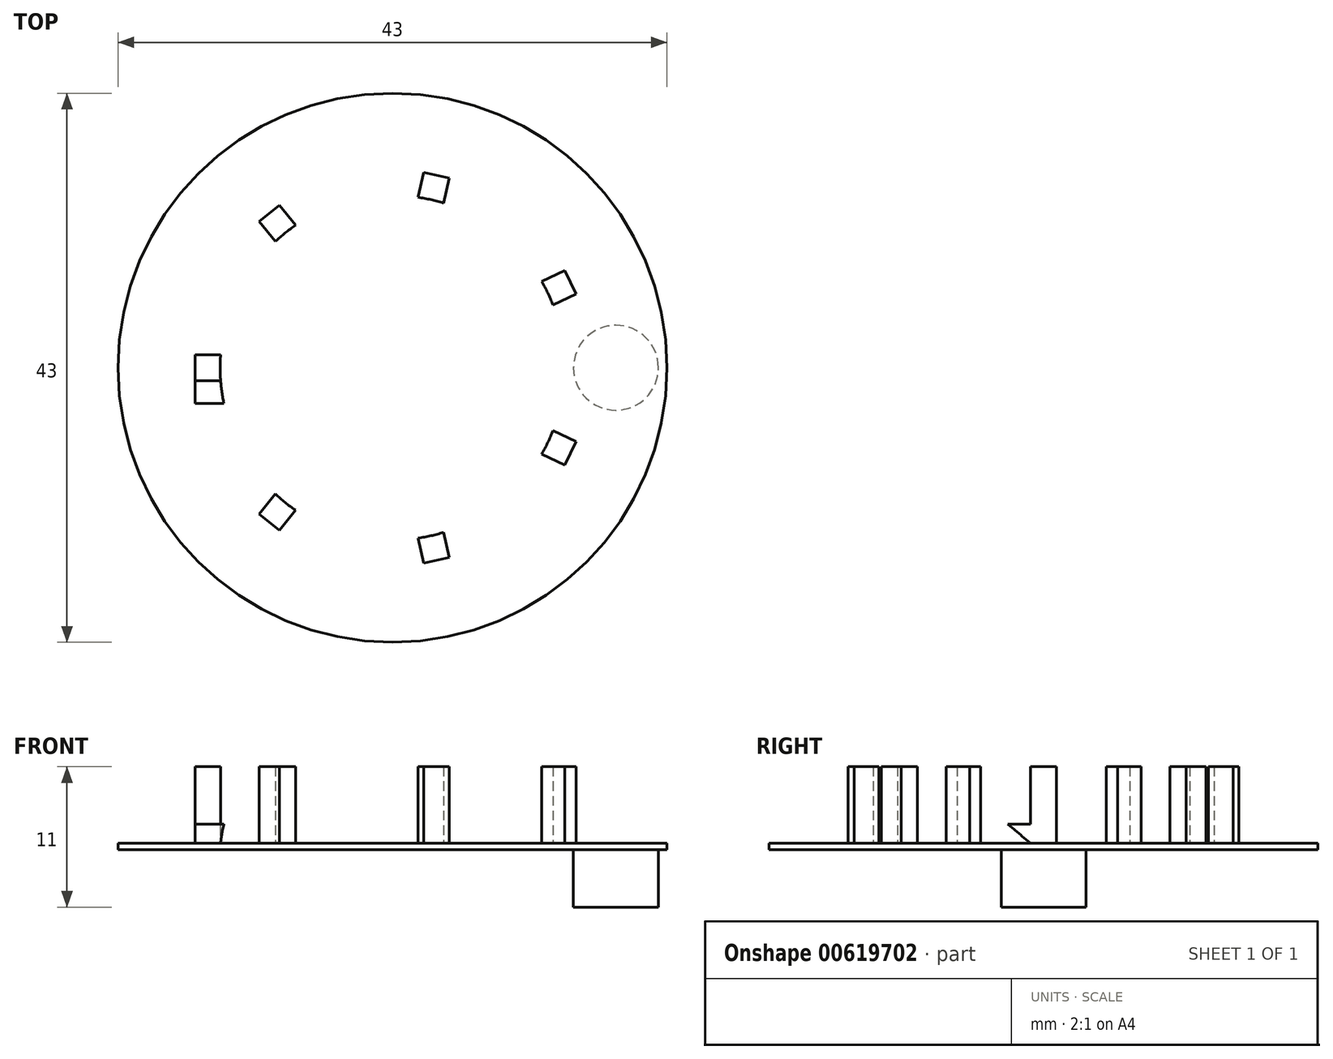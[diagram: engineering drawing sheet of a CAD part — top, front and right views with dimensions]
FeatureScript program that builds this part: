
annotation { "Feature Type Name" : "Feature", "Feature Type Description" : "" }
export const myFeature = defineFeature(function(context is Context, id is Id, definition is map)
    precondition{}
    {
        {
            var Q0;
            Q0=qCreatedBy(makeId("Top.planeOp"),FACE);
            var sketch = newSketch(context, id + "F0", { "sketchPlane" : qUnion([Q0])});
            skCircle(sketch, "E0", {"center": v(0, 0) * mm, "radius": 13.5 * mm});
            skCircle(sketch, "E1", {"center": v(0, 0) * mm, "radius": 21.5 * mm});
            skSolve(sketch);
        }
        {
            var Q0;
            Q0=makeQuery(id+"F0.imprint","IMPRINT",FACE,{"disambiguationData":[TD([[makeQuery(id+"F0.imprint","IMPRINT",EDGE,{"derivedFrom":sQuery(id+"F0.wireOp",EDGE,"E0")}),-1.0]])]});
            var Q1;
            Q1=makeQuery(id+"F0.imprint","IMPRINT",FACE,{"disambiguationData":[TD([[makeQuery(id+"F0.imprint","IMPRINT",EDGE,{"derivedFrom":sQuery(id+"F0.wireOp",EDGE,"E0")}),1.0]])]});
            extrude(context, id + "F1", {"entities" : qUnion([Q0, Q1]), "depth" : 5 * mm, "offsetDistance" : 25 * mm});
        }
        {
            var Q0;
            Q0=makeQuery(id+"F1.opExtrude","CAP_FACE",FACE,{"disambiguationData":[OSD([sQuery(id+"F0.wireOp",EDGE,"E1")])],"isStart":false});
            var sketch = newSketch(context, id + "F2", { "sketchPlane" : qUnion([Q0])});
            skCircle(sketch, "E2", {"center": v(0, 0) * mm, "radius": 13.5 * mm, "construction": true});
            skLineSegment(sketch, "E3.bottom", {"start": v(-13.46, 1.02) * mm, "end": v(-15.46, 1.02) * mm});
            skLineSegment(sketch, "E3.top", {"start": v(-13.46, -1.02) * mm, "end": v(-15.46, -1.02) * mm});
            skLineSegment(sketch, "E3.right", {"start": v(-15.46, 1.02) * mm, "end": v(-15.46, -1.02) * mm});
            skPoint(sketch, "E3.middle", {"position": v(-14.46, 0) * mm});
            skArc(sketch, "E4", {"start": v(-13.46, 1.02) * mm, "mid": v(-13.5, 0) * mm, "end": v(-13.46, -1.02) * mm});
            skArc(sketch, "E5.1.0", {"start": v(-9.19, -9.89) * mm, "mid": v(-8.42, -10.55) * mm, "end": v(-7.6, -11.16) * mm});
            skLineSegment(sketch, "E5.1.1", {"start": v(-10.44, -11.45) * mm, "end": v(-8.84, -12.72) * mm});
            skLineSegment(sketch, "E5.1.2", {"start": v(-7.6, -11.16) * mm, "end": v(-8.84, -12.72) * mm});
            skLineSegment(sketch, "E5.1.3", {"start": v(-9.19, -9.89) * mm, "end": v(-10.44, -11.45) * mm});
            skPoint(sketch, "E5.1.4", {"position": v(-9.02, -11.3) * mm});
            skArc(sketch, "E5.2.0", {"start": v(2, -13.35) * mm, "mid": v(3, -13.16) * mm, "end": v(3.99, -12.9) * mm});
            skLineSegment(sketch, "E5.2.1", {"start": v(2.45, -15.3) * mm, "end": v(4.43, -14.85) * mm});
            skLineSegment(sketch, "E5.2.2", {"start": v(3.99, -12.9) * mm, "end": v(4.43, -14.85) * mm});
            skLineSegment(sketch, "E5.2.3", {"start": v(2, -13.35) * mm, "end": v(2.45, -15.3) * mm});
            skPoint(sketch, "E5.2.4", {"position": v(3.22, -14.1) * mm});
            skArc(sketch, "E5.3.0", {"start": v(11.69, -6.76) * mm, "mid": v(12.16, -5.86) * mm, "end": v(12.57, -4.92) * mm});
            skLineSegment(sketch, "E5.3.1", {"start": v(13.49, -7.63) * mm, "end": v(14.37, -5.8) * mm});
            skLineSegment(sketch, "E5.3.2", {"start": v(12.57, -4.92) * mm, "end": v(14.37, -5.8) * mm});
            skLineSegment(sketch, "E5.3.3", {"start": v(11.69, -6.76) * mm, "end": v(13.49, -7.63) * mm});
            skPoint(sketch, "E5.3.4", {"position": v(13.03, -6.27) * mm});
            skArc(sketch, "E5.4.0", {"start": v(12.57, 4.92) * mm, "mid": v(12.16, 5.86) * mm, "end": v(11.69, 6.76) * mm});
            skLineSegment(sketch, "E5.4.1", {"start": v(14.37, 5.8) * mm, "end": v(13.49, 7.63) * mm});
            skLineSegment(sketch, "E5.4.2", {"start": v(11.69, 6.76) * mm, "end": v(13.49, 7.63) * mm});
            skLineSegment(sketch, "E5.4.3", {"start": v(12.57, 4.92) * mm, "end": v(14.37, 5.8) * mm});
            skPoint(sketch, "E5.4.4", {"position": v(13.03, 6.27) * mm});
            skArc(sketch, "E5.5.0", {"start": v(3.99, 12.9) * mm, "mid": v(3, 13.16) * mm, "end": v(2, 13.35) * mm});
            skLineSegment(sketch, "E5.5.1", {"start": v(4.43, 14.85) * mm, "end": v(2.45, 15.3) * mm});
            skLineSegment(sketch, "E5.5.2", {"start": v(2, 13.35) * mm, "end": v(2.45, 15.3) * mm});
            skLineSegment(sketch, "E5.5.3", {"start": v(3.99, 12.9) * mm, "end": v(4.43, 14.85) * mm});
            skPoint(sketch, "E5.5.4", {"position": v(3.22, 14.1) * mm});
            skArc(sketch, "E5.6.0", {"start": v(-7.6, 11.16) * mm, "mid": v(-8.42, 10.55) * mm, "end": v(-9.19, 9.89) * mm});
            skLineSegment(sketch, "E5.6.1", {"start": v(-8.84, 12.72) * mm, "end": v(-10.44, 11.45) * mm});
            skLineSegment(sketch, "E5.6.2", {"start": v(-9.19, 9.89) * mm, "end": v(-10.44, 11.45) * mm});
            skLineSegment(sketch, "E5.6.3", {"start": v(-7.6, 11.16) * mm, "end": v(-8.84, 12.72) * mm});
            skPoint(sketch, "E5.6.4", {"position": v(-9.02, 11.3) * mm});
            skSolve(sketch);
        }
        {
            var Q0;
            Q0 = qSketchRegion(id + "F2", true);
            extrude(context, id + "F3", {"entities" : qUnion([Q0]), "operationType" : NewBodyOperationType.ADD, "depth" : 6 * mm, "offsetDistance" : 25 * mm});
        }
        {
            var Q0;
            Q0=makeQuery(id+"F1.opExtrude","CAP_FACE",FACE,{"disambiguationData":[OSD([sQuery(id+"F0.wireOp",EDGE,"E1")])],"isStart":true});
            var sketch = newSketch(context, id + "F4", { "sketchPlane" : qUnion([Q0])});
            skCircle(sketch, "E6", {"center": v(-17.5, 0) * mm, "radius": 3.33 * mm});
            skCircle(sketch, "E7.MirrorC", {"center": v(17.5, 0) * mm, "radius": 3.33 * mm});
            skCircle(sketch, "E8", {"center": v(0, 0) * mm, "radius": 13.5 * mm, "construction": true});
            skLineSegment(sketch, "E9", {"start": v(-21.5, 0) * mm, "end": v(-13.5, 0) * mm, "construction": true});
            skSolve(sketch);
        }
        {
            var Q0;
            Q0=makeQuery(id+"F4.imprint","IMPRINT",FACE,{"disambiguationData":[TD([[makeQuery(id+"F4.imprint","IMPRINT",EDGE,{"derivedFrom":sQuery(id+"F4.wireOp",EDGE,"E6")}),1.0]])]});
            var Q1;
            Q1=makeQuery(id+"F4.imprint","IMPRINT",FACE,{"disambiguationData":[TD([[makeQuery(id+"F4.imprint","IMPRINT",EDGE,{"derivedFrom":sQuery(id+"F4.wireOp",EDGE,"E7.MirrorC")}),-1.0]])]});
            extrude(context, id + "F5", {"entities" : qUnion([Q0, Q1]), "operationType" : NewBodyOperationType.REMOVE, "oppositeDirection" : true, "depth" : 4.5 * mm, "offsetDistance" : 25 * mm});
        }
        {
            var Q0;
            Q0=makeQuery(id+"F3.opExtrude","SWEPT_FACE",FACE,{"disambiguationData":[OSD([sQuery(id+"F2.wireOp",EDGE,"E3.right")])]});
            var sketch = newSketch(context, id + "F6", { "sketchPlane" : qUnion([Q0])});
            skLineSegment(sketch, "E10", {"start": v(1.02, 5) * mm, "end": v(2.8, 6.5) * mm});
            skLineSegment(sketch, "E11", {"start": v(2.8, 6.5) * mm, "end": v(1.02, 6.5) * mm});
            skSolve(sketch);
        }
        {
            var Q0;
            {var subQ0=sQuery(id+"F6.wireOp",EDGE,"E10");Q0=makeQuery(id+"F6.imprint","IMPRINT",FACE,{"disambiguationData":[TD([[makeQuery(id+"F6.imprint","IMPRINT",EDGE,{"derivedFrom":subQ0}),1.0]])]});}
            var Q1;
            Q1=makeQuery(id+"F3.opExtrude","SWEPT_FACE",FACE,{"disambiguationData":[OSD([sQuery(id+"F2.wireOp",EDGE,"E4")])]});
            extrude(context, id + "F7", {"entities" : qUnion([Q0]), "operationType" : NewBodyOperationType.ADD, "endBound" : BoundingType.UP_TO_SURFACE, "oppositeDirection" : true, "depth" : 25 * mm, "endBoundEntityFace" : qUnion([Q1]), "offsetDistance" : 25 * mm});
        }
    });
